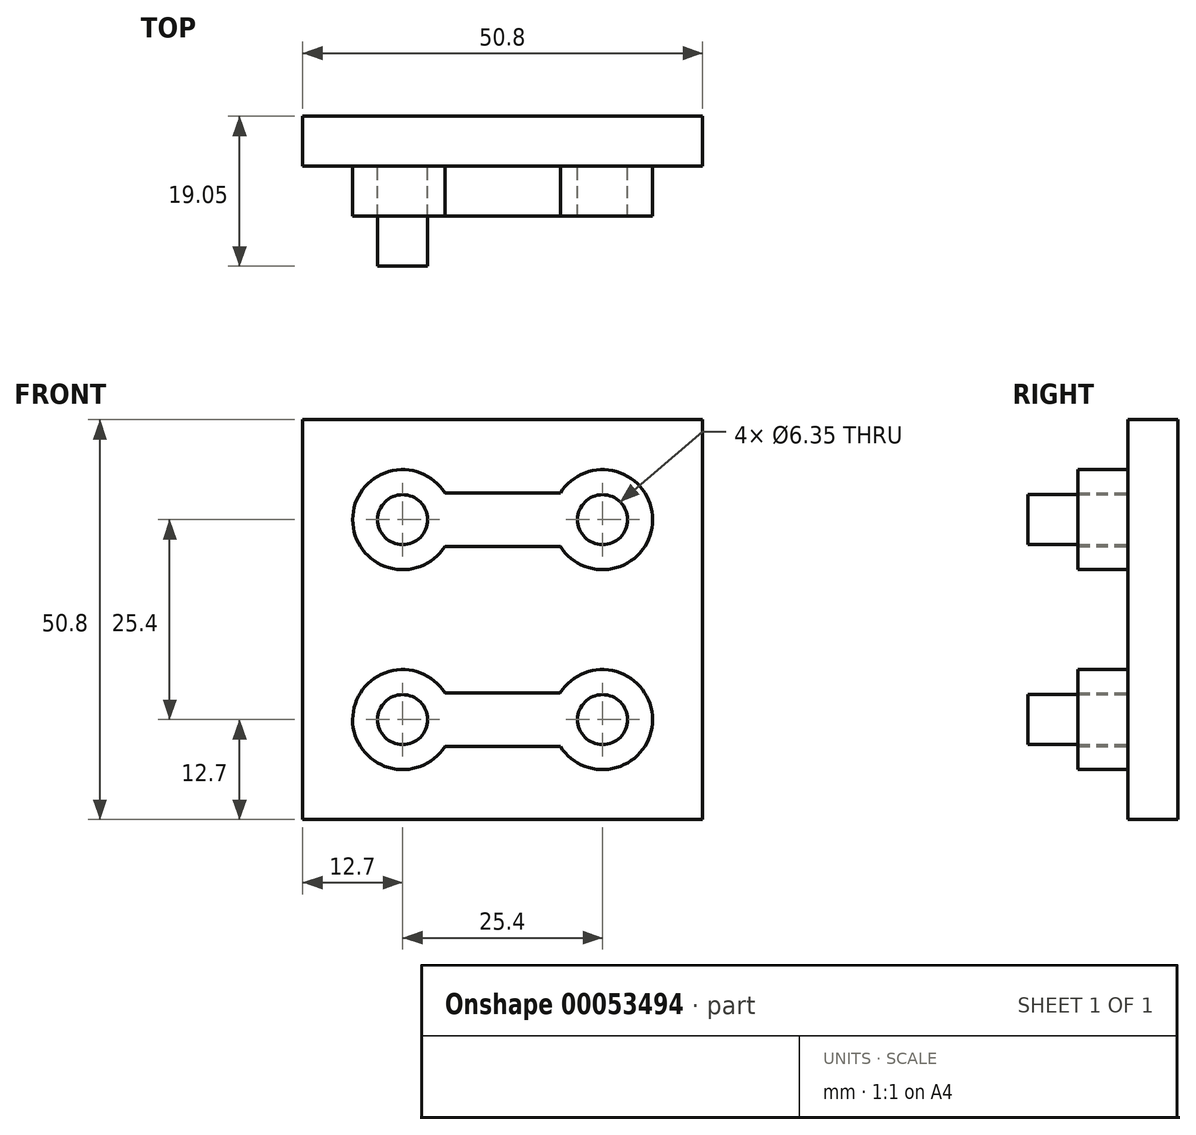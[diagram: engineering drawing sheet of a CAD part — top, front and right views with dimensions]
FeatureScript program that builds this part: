
annotation { "Feature Type Name" : "Feature", "Feature Type Description" : "" }
export const myFeature = defineFeature(function(context is Context, id is Id, definition is map)
    precondition{}
    {
        {
            var Q0;
            Q0=qCreatedBy(makeId("Front.planeOp"),FACE);
            var sketch = newSketch(context, id + "F0", { "sketchPlane" : qUnion([Q0])});
            skLineSegment(sketch, "E0.rect.bottom", {"start": v(25.4, -25.4) * mm, "end": v(-25.4, -25.4) * mm});
            skLineSegment(sketch, "E0.rect.top", {"start": v(25.4, 25.4) * mm, "end": v(-25.4, 25.4) * mm});
            skLineSegment(sketch, "E0.rect.left", {"start": v(25.4, -25.4) * mm, "end": v(25.4, 25.4) * mm});
            skLineSegment(sketch, "E0.rect.right", {"start": v(-25.4, -25.4) * mm, "end": v(-25.4, 25.4) * mm});
            skPoint(sketch, "E0.rect.middle", {"position": v(0, 0) * mm});
            skCircle(sketch, "E1", {"center": v(-12.7, 12.7) * mm, "radius": 3.18 * mm});
            skCircle(sketch, "E2", {"center": v(-12.7, -12.7) * mm, "radius": 3.18 * mm});
            skLineSegment(sketch, "E3", {"start": v(-12.7, 12.7) * mm, "end": v(-12.7, -12.7) * mm, "construction": true});
            skLineSegment(sketch, "E4", {"start": v(-25.4, 0) * mm, "end": v(-12.7, 0) * mm, "construction": true});
            skSolve(sketch);
        }
        {
            var Q0;
            Q0=makeQuery(id+"F0.imprint","IMPRINT",FACE,{"disambiguationData":[TD([[makeQuery(id+"F0.imprint","IMPRINT",EDGE,{"derivedFrom":sQuery(id+"F0.wireOp",EDGE,"E0.rect.bottom")}),-1.0]])]});
            var Q1;
            Q1=makeQuery(id+"F0.imprint","IMPRINT",FACE,{"disambiguationData":[TD([[makeQuery(id+"F0.imprint","IMPRINT",EDGE,{"derivedFrom":sQuery(id+"F0.wireOp",EDGE,"E1")}),1.0]])]});
            var Q2;
            Q2=makeQuery(id+"F0.imprint","IMPRINT",FACE,{"disambiguationData":[TD([[makeQuery(id+"F0.imprint","IMPRINT",EDGE,{"derivedFrom":sQuery(id+"F0.wireOp",EDGE,"E2")}),1.0]])]});
            extrude(context, id + "F1", {"entities" : qUnion([Q0, Q1, Q2]), "oppositeDirection" : true, "depth" : 6.35 * mm});
        }
        {
            var Q0;
            Q0=makeQuery(id+"F0.imprint","IMPRINT",FACE,{"disambiguationData":[TD([[makeQuery(id+"F0.imprint","IMPRINT",EDGE,{"derivedFrom":sQuery(id+"F0.wireOp",EDGE,"E2")}),1.0]])]});
            var Q1;
            Q1=makeQuery(id+"F0.imprint","IMPRINT",FACE,{"disambiguationData":[TD([[makeQuery(id+"F0.imprint","IMPRINT",EDGE,{"derivedFrom":sQuery(id+"F0.wireOp",EDGE,"E1")}),1.0]])]});
            extrude(context, id + "F2", {"entities" : qUnion([Q0, Q1]), "operationType" : NewBodyOperationType.ADD, "depth" : 12.7 * mm});
        }
        {
            var Q0;
            Q0=makeQuery(id+"F1.opExtrude","CAP_FACE",FACE,{"disambiguationData":[OSD([sQuery(id+"F0.wireOp",EDGE,"E0.rect.bottom"),sQuery(id+"F0.wireOp",EDGE,"E0.rect.top"),sQuery(id+"F0.wireOp",EDGE,"E0.rect.left"),sQuery(id+"F0.wireOp",EDGE,"E0.rect.right")])],"isStart":true});
            var sketch = newSketch(context, id + "F3", { "sketchPlane" : qUnion([Q0])});
            skCircle(sketch, "E5.0", {"center": v(-12.7, 12.7) * mm, "radius": 3.18 * mm});
            skCircle(sketch, "E6.0", {"center": v(-12.7, -12.7) * mm, "radius": 3.18 * mm});
            skCircle(sketch, "E7.0", {"center": v(-12.7, 12.7) * mm, "radius": 6.35 * mm});
            skCircle(sketch, "E8.0", {"center": v(-12.7, -12.7) * mm, "radius": 6.35 * mm});
            skLineSegment(sketch, "E9", {"start": v(-12.7, 12.7) * mm, "end": v(-25.4, 12.7) * mm, "construction": true});
            skCircle(sketch, "E10", {"center": v(12.7, 12.7) * mm, "radius": 3.18 * mm});
            skCircle(sketch, "E11", {"center": v(12.7, -12.7) * mm, "radius": 3.18 * mm});
            skCircle(sketch, "E12", {"center": v(12.7, -12.7) * mm, "radius": 6.35 * mm});
            skCircle(sketch, "E13", {"center": v(12.7, 12.7) * mm, "radius": 6.35 * mm});
            skLineSegment(sketch, "E14", {"start": v(-12.7, 12.7) * mm, "end": v(12.7, 12.7) * mm, "construction": true});
            skLineSegment(sketch, "E15", {"start": v(12.7, 12.7) * mm, "end": v(12.7, -12.7) * mm, "construction": true});
            skLineSegment(sketch, "E16", {"start": v(12.7, -12.7) * mm, "end": v(-12.7, -12.7) * mm, "construction": true});
            skLineSegment(sketch, "E17.rect.bottom", {"start": v(7.33, 16.08) * mm, "end": v(-7.33, 16.08) * mm});
            skLineSegment(sketch, "E17.rect.top", {"start": v(7.33, 9.32) * mm, "end": v(-7.33, 9.32) * mm});
            skPoint(sketch, "E17.rect.middle", {"position": v(0, 12.7) * mm});
            skLineSegment(sketch, "E18.rect.bottom", {"start": v(7.32, -9.33) * mm, "end": v(-7.32, -9.33) * mm});
            skLineSegment(sketch, "E18.rect.top", {"start": v(7.33, -16.09) * mm, "end": v(-7.33, -16.09) * mm});
            skSolve(sketch);
        }
        {
            var Q0;
            Q0=makeQuery(id+"F3.imprint","IMPRINT",FACE,{"disambiguationData":[TD([[makeQuery(id+"F3.imprint","IMPRINT",EDGE,{"derivedFrom":sQuery(id+"F3.wireOp",EDGE,"E5.0")}),-1.0]])]});
            var Q1;
            {var subQ0=sQuery(id+"F3.wireOp",EDGE,"E17.rect.bottom");Q1=makeQuery(id+"F3.imprint","IMPRINT",FACE,{"disambiguationData":[TD([[makeQuery(id+"F3.imprint","IMPRINT",EDGE,{"derivedFrom":subQ0}),1.0]])]});}
            var Q2;
            Q2=makeQuery(id+"F3.imprint","IMPRINT",FACE,{"disambiguationData":[TD([[makeQuery(id+"F3.imprint","IMPRINT",EDGE,{"derivedFrom":sQuery(id+"F3.wireOp",EDGE,"E10")}),-1.0]])]});
            var Q3;
            Q3=makeQuery(id+"F3.imprint","IMPRINT",FACE,{"disambiguationData":[TD([[makeQuery(id+"F3.imprint","IMPRINT",EDGE,{"derivedFrom":sQuery(id+"F3.wireOp",EDGE,"E6.0")}),-1.0]])]});
            var Q4;
            {var subQ0=sQuery(id+"F3.wireOp",EDGE,"E18.rect.bottom");Q4=makeQuery(id+"F3.imprint","IMPRINT",FACE,{"disambiguationData":[TD([[makeQuery(id+"F3.imprint","IMPRINT",EDGE,{"derivedFrom":subQ0}),1.0]])]});}
            var Q5;
            Q5=makeQuery(id+"F3.imprint","IMPRINT",FACE,{"disambiguationData":[TD([[makeQuery(id+"F3.imprint","IMPRINT",EDGE,{"derivedFrom":sQuery(id+"F3.wireOp",EDGE,"E11")}),-1.0]])]});
            extrude(context, id + "F4", {"entities" : qUnion([Q0, Q1, Q2, Q3, Q4, Q5]), "depth" : 6.35 * mm});
        }
    });
